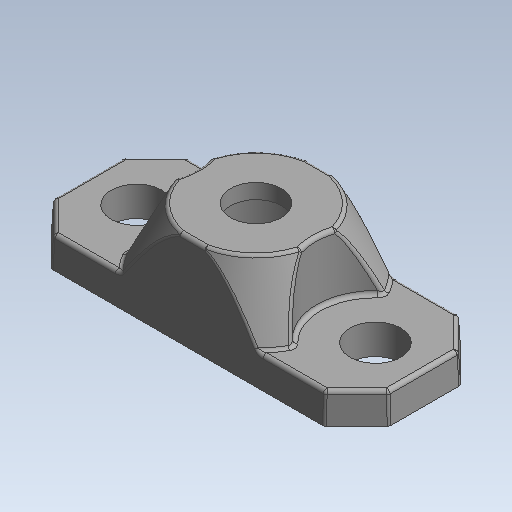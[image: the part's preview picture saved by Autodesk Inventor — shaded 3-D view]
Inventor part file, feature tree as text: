
AUTODESK INVENTOR PART (.ipt)
format: ipt  version: 2020 (Build 240168000, 168)  size: 409,088 bytes
history: native  units: mm (DEFAULTED — no unit token found)
features: fillet x1
ambient origin geometry x8: Origin, YZ Plane, XZ Plane, XY Plane, X Axis, Y Axis, Z Axis, Center Point
bodies: Solid1 (feature_tree)
feature tree (1):
  fillet  "Fillet6"  [1 undecoded]
note: 1 required parameter value undecoded (feature->parameter linkage not recoverable at this tier; creation-order binding heuristic only, values carry confidence <= 0.55)
